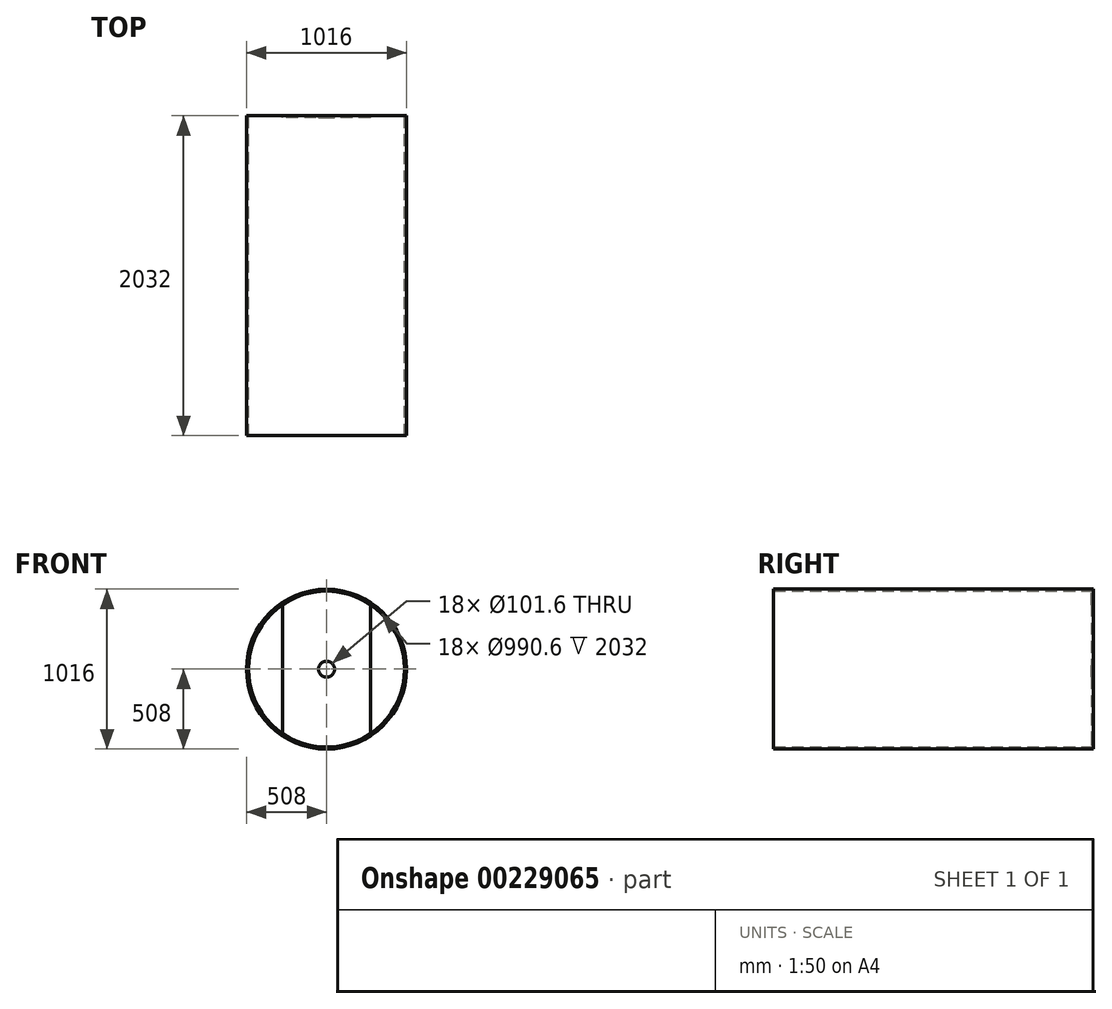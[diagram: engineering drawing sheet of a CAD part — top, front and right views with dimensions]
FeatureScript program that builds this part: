
annotation { "Feature Type Name" : "Feature", "Feature Type Description" : "" }
export const myFeature = defineFeature(function(context is Context, id is Id, definition is map)
    precondition{}
    {
        {
            var Q0;
            Q0=qCreatedBy(makeId("Front.planeOp"),FACE);
            var sketch = newSketch(context, id + "F0", { "sketchPlane" : qUnion([Q0])});
            skCircle(sketch, "E0", {"center": v(0, 0) * mm, "radius": 508 * mm});
            skCircle(sketch, "E1", {"center": v(0, 0) * mm, "radius": 495.3 * mm});
            skLineSegment(sketch, "E2", {"start": v(292.1, 400) * mm, "end": v(292.1, -400) * mm});
            skLineSegment(sketch, "E3", {"start": v(-292.1, 400) * mm, "end": v(-292.1, -400) * mm});
            skLineSegment(sketch, "E4", {"start": v(-279.4, 408.97) * mm, "end": v(-279.4, -408.97) * mm});
            skLineSegment(sketch, "E5", {"start": v(279.4, -408.97) * mm, "end": v(279.4, 408.97) * mm});
            skCircle(sketch, "E6", {"center": v(0, 0) * mm, "radius": 50.8 * mm});
            skSolve(sketch);
        }
        {
            var Q0;
            Q0=makeQuery(id+"F0.imprint","IMPRINT",FACE,{"disambiguationData":[TD([[makeQuery(id+"F0.imprint","IMPRINT",EDGE,{"derivedFrom":sQuery(id+"F0.wireOp",EDGE,"E0")}),1.0]])]});
            extrude(context, id + "F1", {"entities" : qUnion([Q0]), "depth" : 2032 * mm});
        }
        {
            var Q0;
            {var subQ0=sQuery(id+"F0.wireOp",EDGE,"E4");Q0=makeQuery(id+"F0.imprint","IMPRINT",FACE,{"disambiguationData":[TD([[makeQuery(id+"F0.imprint","IMPRINT",EDGE,{"derivedFrom":subQ0}),1.0]])]});}
            extrude(context, id + "F2", {"entities" : qUnion([Q0]), "depth" : 12.7 * mm});
        }
        {
            var Q0;
            Q0=makeQuery(id+"F0.imprint","IMPRINT",FACE,{"disambiguationData":[TD([[makeQuery(id+"F0.imprint","IMPRINT",EDGE,{"derivedFrom":sQuery(id+"F0.wireOp",EDGE,"E6")}),1.0]])]});
            extrude(context, id + "F3", {"entities" : qUnion([Q0]), "operationType" : NewBodyOperationType.REMOVE, "depth" : 25.4 * mm});
        }
    });
